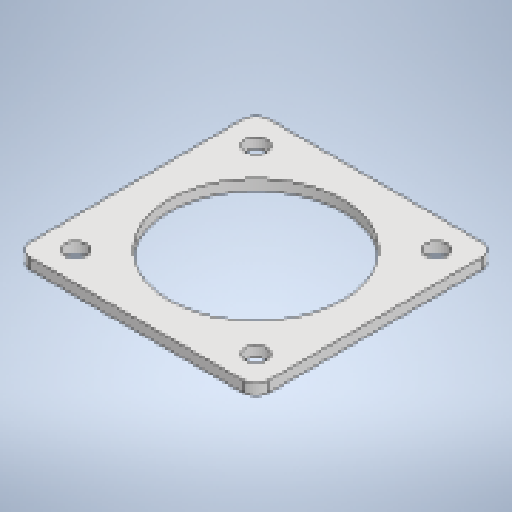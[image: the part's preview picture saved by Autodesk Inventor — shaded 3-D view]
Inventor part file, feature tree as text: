
AUTODESK INVENTOR PART (.ipt)
format: ipt  version: 2025.1 (Build 291241020, 241B)  size: 265,728 bytes
history: native  units: mm
features: sketch x6, sheet_metal_op x4, extrude x3, other x3, pattern_linear x2, chamfer x1, projected_geometry x1
ambient origin geometry x8: Origin, YZ Plane, XZ Plane, XY Plane, X Axis, Y Axis, Z Axis, Center Point
bodies: Solid1 (feature_tree)
feature tree (20):
  sheet_metal_op  "Face1"
  sheet_metal_op  "Flange2"
  extrude  "Extrusion2"  Depth=5.0mm
  pattern_linear  "Rectangular Pattern1"  Count1=20  [1 undecoded]
  extrude  "Extrusion3"  Depth=5.0mm
  pattern_linear  "Rectangular Pattern2"  Count1=5 Spacing1=90.0deg
  extrude  "Extrusion4"  Depth=5.0mm
  chamfer  "Corner Round1"
  sketch  "Sketch1"  dims[d2=5.0mm d25=400.0mm d26=200.0mm]
  other  "Plate1"
  sketch  "Sketch5"  dims[d27=5.0mm d28=2.5mm]
  other  "Plate3"
  sheet_metal_op  "Bend2"
  sheet_metal_op  "Corner2"
  sketch  "Sketch6"  dims[d29=10.0mm]
  sketch  "Sketch7"  dims[d30=5.0mm d31=50.0mm d32=90.0deg d33=5.0mm]
  projected_geometry  "Projected Loop2"
  sketch  "Sketch8"  dims[d34=20.0mm d35=1.0mm d36=5.0mm]
  sketch  "Sketch9"  dims[d37=32.0mm d38=150.0mm d39=5.0mm d40=0.0mm d41=13.0mm d42=25.0mm d43=0.0mm d44=0.0mm d45=30.0mm d47=160.0mm d48=13.0mm d49=25.0mm d50=0.0mm d51=0.0mm d52=30.0mm d54=70.0mm d55=10.0mm d56=83.0mm d57=83.0mm d58=110.0mm d59=110.0mm d60=80.0mm d61=0.0mm d62=0.0mm d63=6.0mm]
  other  "Cut1"
note: 1 required parameter value undecoded (feature->parameter linkage not recoverable at this tier; creation-order binding heuristic only, values carry confidence <= 0.55)
